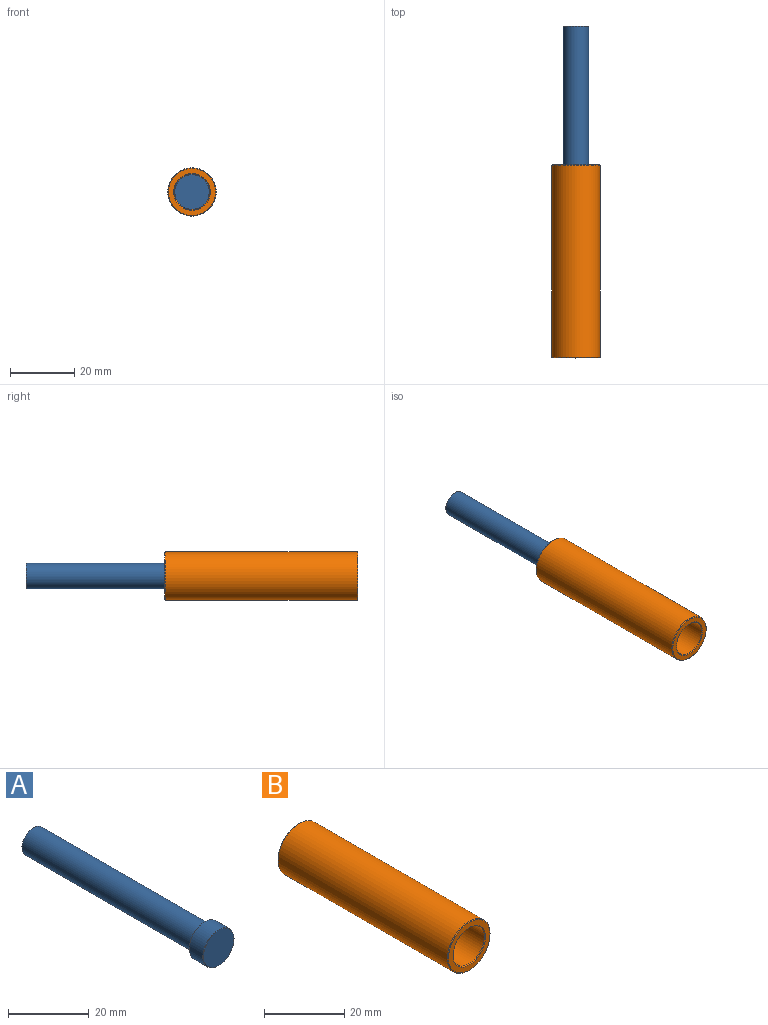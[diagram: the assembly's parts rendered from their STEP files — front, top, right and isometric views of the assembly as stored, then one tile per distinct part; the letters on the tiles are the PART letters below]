
ASSEMBLY  parts=2 mates=1
PART A: 10 faces, bbox 10.9x65x10.9 mm
  f0: cylinder r=4mm len=59.9mm, axis (0,1,0), area 1505.5mm2, adj f4,f7
  f1: plane 7.8x7.8mm, normal (0,1,0), area 28.1mm2, adj f5,f7
  f2: cylinder r=5.45mm len=10.9mm, axis (0,1,0), area 164.4mm2, adj f8,f9
  f3: plane 10.7x10.7mm, normal (0,-1,0), area 89.9mm2, adj f9
  f4: plane 10.7x10.7mm, normal (0,1,0), area 39.7mm2, adj f0,f8
  f5: cylinder r=2.5mm len=20mm, axis (0,1,0), area 314.2mm2, adj f1,f6
  f6: plane 5x5mm, normal (0,1,0), area 19.6mm2, adj f5
  f7: cone r=4mm half-angle=45deg, axis (0,-1,0), area 3.5mm2, adj f0,f1
  f8: cone r=5.45mm half-angle=45deg, axis (0,-1,0), area 4.8mm2, adj f2,f4
  f9: cone r=5.35mm half-angle=45deg, axis (0,1,0), area 4.8mm2, adj f2,f3
PART B: 10 faces, bbox 15x60x15 mm
  f0: cylinder r=5.5mm len=54.8mm, axis (0,1,0), area 1893.8mm2, adj f5,f6
  f1: cylinder r=7.5mm len=59.6mm, axis (0,1,0), area 2808.6mm2, adj f7,f9
  f2: plane 14.6x14.6mm, normal (0,-1,0), area 65.3mm2, adj f6,f7
  f3: plane 14.6x14.6mm, normal (0,1,0), area 109.3mm2, adj f8,f9
  f4: cylinder r=4.1mm len=8.2mm, axis (0,1,0), area 123.7mm2, adj f5,f8
  f5: plane 11x11mm, normal (0,-1,0), area 42.2mm2, adj f0,f4
  f6: cone r=5.5mm half-angle=45deg, axis (0,-1,0), area 10mm2, adj f0,f2
  f7: cone r=7.3mm half-angle=45deg, axis (0,1,0), area 13.2mm2, adj f1,f2
  f8: cone r=4.3mm half-angle=45deg, axis (0,1,0), area 7.5mm2, adj f3,f4
  f9: cone r=7.5mm half-angle=45deg, axis (0,-1,0), area 13.2mm2, adj f1,f3
PLACE A t=(38.29,11.62,-56.01)mm
PLACE B t=(38.29,-31.47,-56.01)mm
MATE slider A.f2 <-> B.f0  axis (0,1,0) through (38.29,-48.48,-56.01)mm
